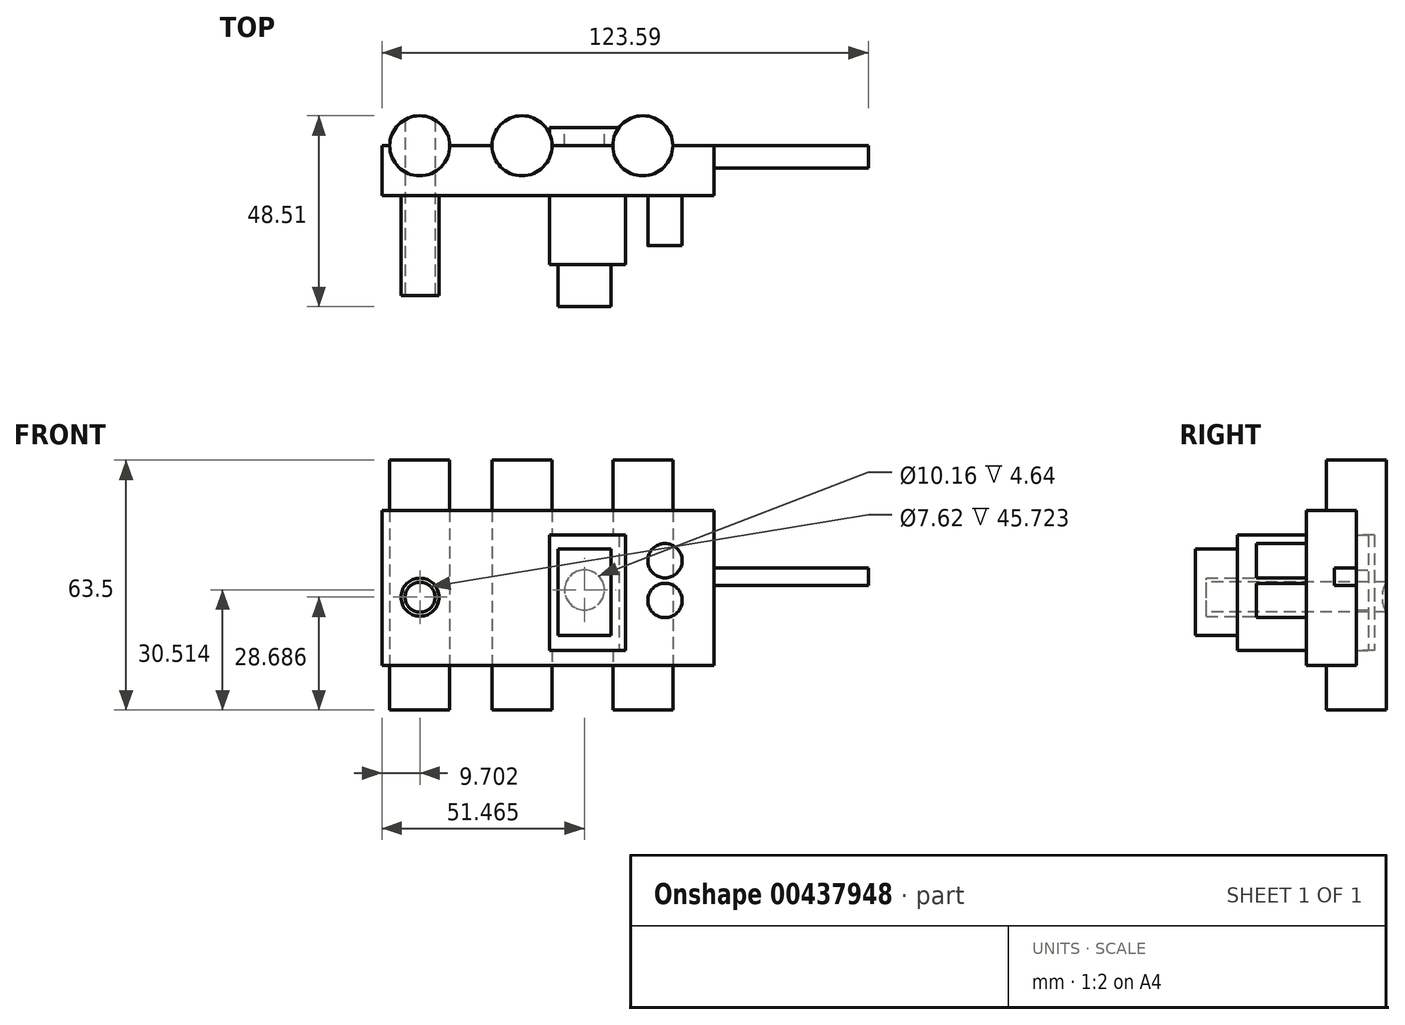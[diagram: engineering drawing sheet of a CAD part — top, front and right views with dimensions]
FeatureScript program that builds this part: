
annotation { "Feature Type Name" : "Feature", "Feature Type Description" : "" }
export const myFeature = defineFeature(function(context is Context, id is Id, definition is map)
    precondition{}
    {
        {
            var Q0;
            Q0=qCreatedBy(makeId("Front.planeOp"),FACE);
            var sketch = newSketch(context, id + "F0", { "sketchPlane" : qUnion([Q0])});
            skLineSegment(sketch, "E0.bottom", {"start": v(22.5, 11.39) * mm, "end": v(-61.87, 11.39) * mm});
            skLineSegment(sketch, "E0.top", {"start": v(22.5, 50.76) * mm, "end": v(-61.87, 50.76) * mm});
            skLineSegment(sketch, "E0.left", {"start": v(22.5, 11.39) * mm, "end": v(22.5, 50.76) * mm});
            skLineSegment(sketch, "E0.right", {"start": v(-61.87, 11.39) * mm, "end": v(-61.87, 50.76) * mm});
            skPoint(sketch, "E0.middle", {"position": v(-19.69, 31.08) * mm});
            skSolve(sketch);
        }
        {
            var Q0;
            Q0 = qSketchRegion(id + "F0", true);
            extrude(context, id + "F1", {"entities" : qUnion([Q0]), "depth" : 12.7 * mm});
        }
        {
            var Q0;
            Q0=qCreatedBy(makeId("Front.planeOp"),FACE);
            var sketch = newSketch(context, id + "F2", { "sketchPlane" : qUnion([Q0])});
            skCircle(sketch, "E1", {"center": v(-26.97, 30.95) * mm, "radius": 12.7 * mm});
            skSolve(sketch);
        }
        {
            var Q0;
            Q0 = qSketchRegion(id + "F2", true);
            var Q1;
            Q1=sQuery(id+"F2.wireOp",EDGE,"E1");
            extrude(context, id + "F3", {"entities" : qUnion([Q0]), "bodyType" : ToolBodyType.SURFACE, "surfaceEntities" : qUnion([Q1]), "depth" : 25.4 * mm});
        }
        {
            var Q0;
            Q0=qCreatedBy(makeId("Right.planeOp"),FACE);
            var sketch = newSketch(context, id + "F4", { "sketchPlane" : qUnion([Q0])});
            skLineSegment(sketch, "E2.bottom", {"start": v(-5.62, 31.62) * mm, "end": v(0, 31.62) * mm});
            skLineSegment(sketch, "E2.top", {"start": v(-5.62, 36.14) * mm, "end": v(0, 36.14) * mm});
            skLineSegment(sketch, "E2.left", {"start": v(-5.62, 31.62) * mm, "end": v(-5.62, 36.14) * mm});
            skLineSegment(sketch, "E2.right", {"start": v(0, 31.62) * mm, "end": v(0, 36.14) * mm});
            skSolve(sketch);
        }
        {
            var Q0;
            Q0 = qSketchRegion(id + "F4", true);
            extrude(context, id + "F5", {"entities" : qUnion([Q0]), "operationType" : NewBodyOperationType.ADD, "depth" : 61.72 * mm});
        }
        {
            var Q0;
            Q0=qCreatedBy(makeId("Top.planeOp"),FACE);
            var sketch = newSketch(context, id + "F6", { "sketchPlane" : qUnion([Q0])});
            skCircle(sketch, "E3", {"center": v(-52.25, 0) * mm, "radius": 7.62 * mm});
            skCircle(sketch, "E4", {"center": v(-26.27, 0) * mm, "radius": 7.62 * mm});
            skCircle(sketch, "E5", {"center": v(4.43, 0) * mm, "radius": 7.62 * mm});
            skSolve(sketch);
        }
        {
            var Q0;
            Q0 = qSketchRegion(id + "F6", true);
            var Q1;
            Q1=sQuery(id+"F6.wireOp",EDGE,"E3");
            var Q2;
            Q2=sQuery(id+"F6.wireOp",EDGE,"E4");
            var Q3;
            Q3=sQuery(id+"F6.wireOp",EDGE,"E5");
            extrude(context, id + "F7", {"entities" : qUnion([Q0]), "operationType" : NewBodyOperationType.ADD, "surfaceEntities" : qUnion([Q1, Q2, Q3]), "depth" : 63.5 * mm});
        }
        {
            var Q0;
            Q0=qCreatedBy(makeId("Front.planeOp"),FACE);
            var sketch = newSketch(context, id + "F8", { "sketchPlane" : qUnion([Q0])});
            skCircle(sketch, "E6", {"center": v(-52.17, 28.69) * mm, "radius": 4.84 * mm});
            skSolve(sketch);
        }
        {
            var Q0;
            Q0 = qSketchRegion(id + "F8", true);
            extrude(context, id + "F9", {"entities" : qUnion([Q0]), "operationType" : NewBodyOperationType.ADD, "depth" : 38.1 * mm});
        }
        {
            var Q0;
            Q0=makeQuery(id+"F9.opExtrude","CAP_FACE",FACE,{"disambiguationData":[OSD([sQuery(id+"F8.wireOp",EDGE,"E6")])],"isStart":false});
            var sketch = newSketch(context, id + "F10", { "sketchPlane" : qUnion([Q0])});
            skCircle(sketch, "E7", {"center": v(-52.17, 28.69) * mm, "radius": 3.38 * mm});
            skSolve(sketch);
        }
        {
            var Q0;
            Q0=sQuery(id+"F10.wireOp",VERTEX,"E7.center");
            var Q1;
            Q1=makeQuery(id+"F1.opExtrude","SWEPT_BODY",BODY,{"disambiguationData":[OSD([sQuery(id+"F0.wireOp",EDGE,"E0.bottom"),sQuery(id+"F0.wireOp",EDGE,"E0.top"),sQuery(id+"F0.wireOp",EDGE,"E0.left"),sQuery(id+"F0.wireOp",EDGE,"E0.right")])]});
            hole(context, id + "F11", {"style" : HoleStyle.SIMPLE, "endStyle" : HoleEndStyle.THROUGH, "holeDiameter" : 7.62 * mm, "isTappedThrough" : true, "tappedDepth" : 12.7 * mm, "tapClearance" : 3, "startFromSketch" : true, "locations" : qUnion([Q0]), "scope" : qUnion([Q1])});
        }
        {
            var Q0;
            Q0=makeQuery(id+"F3.opExtrude","SWEPT_BODY",BODY,{"disambiguationData":[OSD([sQuery(id+"F2.wireOp",EDGE,"E1")])]});
            deleteBodies(context, id + "F12", {"entities" : qUnion([Q0])});
        }
        {
            var Q0;
            Q0=qCreatedBy(makeId("Right.planeOp"),FACE);
            var sketch = newSketch(context, id + "F13", { "sketchPlane" : qUnion([Q0])});
            skLineSegment(sketch, "E8.bottom", {"start": v(4.64, 15.2) * mm, "end": v(-30.23, 15.2) * mm});
            skLineSegment(sketch, "E8.top", {"start": v(4.64, 44.45) * mm, "end": v(-30.23, 44.45) * mm});
            skLineSegment(sketch, "E8.left", {"start": v(4.64, 15.2) * mm, "end": v(4.64, 44.45) * mm});
            skLineSegment(sketch, "E8.right", {"start": v(-30.23, 15.2) * mm, "end": v(-30.23, 44.45) * mm});
            skPoint(sketch, "E8.middle", {"position": v(-12.8, 29.83) * mm});
            skSolve(sketch);
        }
        {
            var Q0;
            Q0 = qSketchRegion(id + "F13", true);
            extrude(context, id + "F14", {"entities" : qUnion([Q0]), "operationType" : NewBodyOperationType.ADD, "oppositeDirection" : true, "depth" : 19.3 * mm});
        }
        {
            var Q0;
            Q0=makeQuery(id+"F14.opExtrude","SWEPT_FACE",FACE,{"disambiguationData":[OSD([sQuery(id+"F13.wireOp",EDGE,"E8.left")])]});
            var sketch = newSketch(context, id + "F15", { "sketchPlane" : qUnion([Q0])});
            skCircle(sketch, "E9", {"center": v(10.4, 30.51) * mm, "radius": 4.45 * mm});
            skSolve(sketch);
        }
        {
            var Q0;
            Q0=sQuery(id+"F15.wireOp",VERTEX,"E9.center");
            var Q1;
            Q1=makeQuery(id+"F1.opExtrude","SWEPT_BODY",BODY,{"disambiguationData":[OSD([sQuery(id+"F0.wireOp",EDGE,"E0.bottom"),sQuery(id+"F0.wireOp",EDGE,"E0.top"),sQuery(id+"F0.wireOp",EDGE,"E0.left"),sQuery(id+"F0.wireOp",EDGE,"E0.right")])]});
            hole(context, id + "F16", {"style" : HoleStyle.SIMPLE, "endStyle" : HoleEndStyle.THROUGH, "holeDiameter" : 10.16 * mm, "isTappedThrough" : true, "tappedDepth" : 12.7 * mm, "tapClearance" : 3, "startFromSketch" : true, "locations" : qUnion([Q0]), "scope" : qUnion([Q1])});
        }
        {
            var Q0;
            Q0=qCreatedBy(makeId("Front.planeOp"),FACE);
            var sketch = newSketch(context, id + "F17", { "sketchPlane" : qUnion([Q0])});
            skLineSegment(sketch, "E10.bottom", {"start": v(-3.66, 18.98) * mm, "end": v(-17.16, 18.98) * mm});
            skLineSegment(sketch, "E10.top", {"start": v(-3.66, 40.91) * mm, "end": v(-17.16, 40.91) * mm});
            skLineSegment(sketch, "E10.left", {"start": v(-3.66, 18.98) * mm, "end": v(-3.66, 40.91) * mm});
            skLineSegment(sketch, "E10.right", {"start": v(-17.16, 18.98) * mm, "end": v(-17.16, 40.91) * mm});
            skPoint(sketch, "E10.middle", {"position": v(-10.4, 29.95) * mm});
            skSolve(sketch);
        }
        {
            var Q0;
            Q0 = qSketchRegion(id + "F17", true);
            extrude(context, id + "F18", {"entities" : qUnion([Q0]), "operationType" : NewBodyOperationType.ADD, "depth" : 40.9 * mm});
        }
        {
            var Q0;
            Q0=qCreatedBy(makeId("Front.planeOp"),FACE);
            var sketch = newSketch(context, id + "F19", { "sketchPlane" : qUnion([Q0])});
            skCircle(sketch, "E11", {"center": v(10.06, 27.86) * mm, "radius": 4.37 * mm});
            skCircle(sketch, "E12", {"center": v(10.06, 37.97) * mm, "radius": 4.37 * mm});
            skSolve(sketch);
        }
        {
            var Q0;
            Q0 = qSketchRegion(id + "F19", true);
            extrude(context, id + "F20", {"entities" : qUnion([Q0]), "operationType" : NewBodyOperationType.ADD, "depth" : 25.4 * mm});
        }
    });
